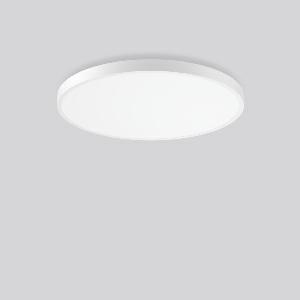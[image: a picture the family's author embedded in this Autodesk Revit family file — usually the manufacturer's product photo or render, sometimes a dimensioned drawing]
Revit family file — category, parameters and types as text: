
# Revit family: triona_round_a_312387_002_730_4d29
name_source: partatom
category: Lighting Fixtures
units: mm (PartAtom-declared; Revit-internal decimal feet)

## family parameters
Cut with Voids When Loaded = No
Host = Face
Light Source = No
Part Type = Normal
Room Calculation Point = No
Round Connector Dimension = Use Diameter
Shared = No

## types (1)
- TRIONA round A (1 x LED Modul 830, 8000 lm, 3000)
    Apparent Load = 80 VA
    CIE Flux Codes = 49 80 96 100 100
    Color Rendering = 80
    Color Temperature = 3000
    Default Elevation = 1800 mm
    Description = Series: TRIONA round
Decorative round LED surface-mounted luminaire. Flat, seamless frame: aluminium extrusion profile, powder coated. Cover made of sheet steel, powder-coated. Light emission through a diffuser: plastic, opal. Lightguide and diffuser made of non-yellowing plastic (PMMA). Lateral light emission (RZB SIDELITE technology) for above-average homogeneous light distribution. Suitable for Ceiling mounting, Wall (surface). Tool-free mounting via bayonet connection. Electronic ballast included. Very easy installation thanks to Plug+Play connection. With Casambi smart+free Bluetooth control for wireless network and operation using Android / iOS devices, free app available for download. 
Colour: traffic white, matt (RAL 9016)
Diameter: 845 mm
Height: 88 mm
Lamp: LED
Socket: without socket
Colour temperature: 3000K
Colour rendering index (CRI): 80
System power: 80 W
Rated luminous flux: 8000 lm
Luminous efficiency: 100 lm/W
Control gear: Dimmable Bluetooth converter
Protection class: I
Type of protection: IP 20
    Height = 88 mm
    Lamp = 1 x LED Modul 830
    Lamp Light Flux = 8000 lm
    Lamp count = 1
    Length = 845 mm
    Lifetime = 50000 h
    Luminous efficacy = 100 lm/W
    Manufacturer = RZB
    ModVariant = No
    Model = 312387.002.730
    Mounting Place = Ceiling
    Mounting Type = Surface mounted
    Number of Poles = 1
    OnlyDefault = Yes
    Power Factor = 1
    Product Name = TRIONA round A
    Product group = Surface mounted modular luminaires
    ProductGroupID = 306
    Protection Class = Protection class I
    Protection Degree = IP 20
    RLX_Detail_Level = 1
    RLX_Emergency_Light_Flux = 0 lm
    RLX_Emergency_Type = 0
    RLX_Emergency_Type_DB = No
    RlxData = <blob elided: 32457 chars, md5=7bb2203f>
    Socket = socket
    Standby Power = 0 W
    System Light Flux = 8000 lm
    System Power = 80 W
    Type Comments = Product without accessories
    Type Image = 312388.002.jpg
    URL = http://relux.com
    VarID = ---
    Voltage = 230 V
    Voltage Range = 220-240 V
    Weight = 0.00 kg
    Width = 0 mm  [stored 0 ft]

note: [stored X ft] marks values corroborated as IEEE doubles in the binary element streams (Revit-internal decimal feet)

## geometry (parser evidence)
native form markers: Blend x4, Sweep x10
no freeform markers — native parametric forms only
